# Revit family: HERZ Commissioning Valve With Metering Station For Drinking Water Systems 4017 MW (LF-MF)
name_source: partatom
category: Rohrzubehör
revit_build: Autodesk Revit 2018 (Build: 20190510_1515(x64)
units: mm (PartAtom-declared; Revit-internal decimal feet)

## family parameters
Arbeitsebenenbasiert = Nein
Beim Laden mit Abzugskörper schneiden = Nein
Bemaßung runder Anschluss = Durchmesser verwenden
Gemeinsam genutzt = Nein
Immer vertikal = Ja
OmniClass-Nummer = 23.65.55.14
OmniClass-Titel = Valves for Liquid Services
Teiletyp = Unterbricht

## types (2) — shared parameters
Application = For shutting off and regulating drinking water systems in buildings or for hydraulic balancing of supply lines.
Body = DZR brass
H02 = 13 mm
Hand wheel = plastic, green
Hersteller = HERZ Armaturen Ges.m.b.H.
Max. differential pressure on closed seat = 1000000.0 Pa
Max. operating pressure at 20°C = 2000000.0 Pa
Max. operating temperature at 10 bar = 85 °C
Medium = Water
Model = According to standard BS 7350 PN20 Series B
Angle seat regulating valve made of copper alloy.
All metal parts in contact with water are made of dezincification-resistant copper alloy.
The upper parts are equipped with non-rising stem.
Note = Pursuant to Article 33 of the REACH Regulation (EC No. 1907/2006), we are obliged to point out that the material lead is listed on the SVHC list and that all brass components manufactured in our products exceed 0.1% (w / w) lead (CAS: 7439-92-1 / EINECS: 231-100-4).
Since lead is a component part of an alloy, actual exposure is not possible and therefore no additional information on safe use is necessary.
O-Rings = EPDM
R01 = 12 mm  [stored 0.0393701 ft]
R02 = 9.5 mm  [stored 0.031168 ft]
R03 = 21.5 mm  [stored 0.0705381 ft]
S03 = 60 mm  [stored 0.19685 ft]
SCRNCODE = 04;00;02
SCRNSEQ = FW;SBT_TYP_FW="109";2
SW01 = 60.00°
URL = www.herzvalves.com
W01 = 45.00°
zero-valued in all types: E00

## per-type parameters (varying)
| type | LF | MF |
| LF | Ja | Nein |
| MF | Nein | Ja |

note: [stored X ft] marks values corroborated as IEEE doubles in the binary element streams (Revit-internal decimal feet)
